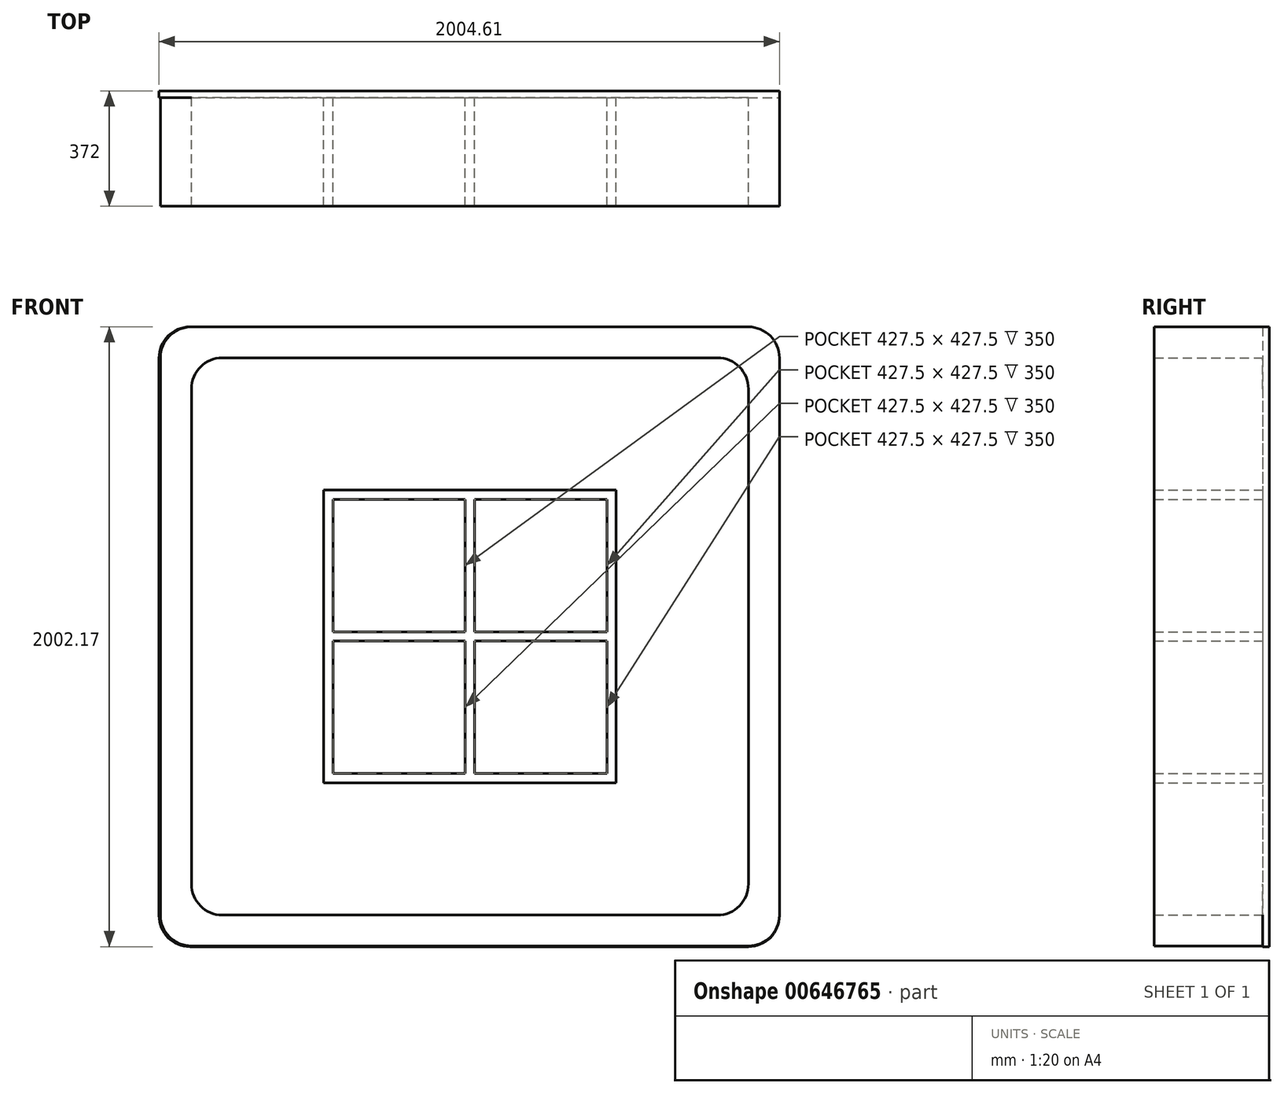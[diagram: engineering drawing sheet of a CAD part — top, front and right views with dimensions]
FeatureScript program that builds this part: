
annotation { "Feature Type Name" : "Feature", "Feature Type Description" : "" }
export const myFeature = defineFeature(function(context is Context, id is Id, definition is map)
    precondition{}
    {
        {
            var Q0;
            Q0=qCreatedBy(makeId("Front.planeOp"),FACE);
            var sketch = newSketch(context, id + "F0", { "sketchPlane" : qUnion([Q0])});
            skLineSegment(sketch, "E0.bottom", {"start": v(-1413.67, 1120.62) * mm, "end": v(386.33, 1120.62) * mm});
            skLineSegment(sketch, "E0.top", {"start": v(-1413.67, -879.38) * mm, "end": v(386.33, -879.38) * mm});
            skLineSegment(sketch, "E0.left", {"start": v(-1513.67, 1020.62) * mm, "end": v(-1513.67, -779.38) * mm});
            skLineSegment(sketch, "E0.right", {"start": v(486.33, 1020.62) * mm, "end": v(486.33, -779.38) * mm});
            skLineSegment(sketch, "E1.bottom", {"start": v(-1313.67, 1020.62) * mm, "end": v(286.33, 1020.62) * mm});
            skLineSegment(sketch, "E1.top", {"start": v(-1313.67, -779.38) * mm, "end": v(286.33, -779.38) * mm});
            skLineSegment(sketch, "E1.left", {"start": v(-1413.67, 920.62) * mm, "end": v(-1413.67, -679.38) * mm});
            skLineSegment(sketch, "E1.right", {"start": v(386.33, 920.62) * mm, "end": v(386.33, -679.38) * mm});
            skPoint(sketch, "E2.visualSharp", {"position": v(-1513.67, 1120.62) * mm});
            skArc(sketch, "E2.filletArc", {"start": v(-1413.67, 1120.62) * mm, "mid": v(-1484.38, 1091.33) * mm, "end": v(-1513.67, 1020.62) * mm});
            skArc(sketch, "E3.filletArc", {"start": v(-1313.67, 1020.62) * mm, "mid": v(-1384.38, 991.33) * mm, "end": v(-1413.67, 920.62) * mm});
            skPoint(sketch, "E4.visualSharp", {"position": v(486.33, 1120.62) * mm});
            skArc(sketch, "E4.filletArc", {"start": v(486.33, 1020.62) * mm, "mid": v(457.05, 1091.33) * mm, "end": v(386.33, 1120.62) * mm});
            skArc(sketch, "E5.filletArc", {"start": v(386.33, 920.62) * mm, "mid": v(357.05, 991.33) * mm, "end": v(286.33, 1020.62) * mm});
            skPoint(sketch, "E6.visualSharp", {"position": v(386.33, -779.38) * mm});
            skArc(sketch, "E6.filletArc", {"start": v(286.33, -779.38) * mm, "mid": v(357.05, -750.1) * mm, "end": v(386.33, -679.38) * mm});
            skPoint(sketch, "E7.visualSharp", {"position": v(-1413.67, -779.38) * mm});
            skArc(sketch, "E7.filletArc", {"start": v(-1413.67, -679.38) * mm, "mid": v(-1384.38, -750.1) * mm, "end": v(-1313.67, -779.38) * mm});
            skPoint(sketch, "E8.visualSharp", {"position": v(-1513.67, -879.38) * mm});
            skArc(sketch, "E8.filletArc", {"start": v(-1513.67, -779.38) * mm, "mid": v(-1484.38, -850.1) * mm, "end": v(-1413.67, -879.38) * mm});
            skPoint(sketch, "E9.visualSharp", {"position": v(486.33, -879.38) * mm});
            skArc(sketch, "E9.filletArc", {"start": v(386.33, -879.38) * mm, "mid": v(457.05, -850.1) * mm, "end": v(486.33, -779.38) * mm});
            skLineSegment(sketch, "E10.bottom", {"start": v(-1413.67, 593.12) * mm, "end": v(386.33, 593.12) * mm});
            skLineSegment(sketch, "E10.top", {"start": v(-1413.67, 563.12) * mm, "end": v(386.33, 563.12) * mm});
            skLineSegment(sketch, "E10.left", {"start": v(-1413.67, 593.12) * mm, "end": v(-1413.67, 563.12) * mm});
            skLineSegment(sketch, "E10.right", {"start": v(386.33, 593.12) * mm, "end": v(386.33, 563.12) * mm});
            skLineSegment(sketch, "E11.bottom", {"start": v(-1413.67, 135.62) * mm, "end": v(386.33, 135.62) * mm});
            skLineSegment(sketch, "E11.top", {"start": v(-1413.67, 105.62) * mm, "end": v(386.33, 105.62) * mm});
            skLineSegment(sketch, "E11.left", {"start": v(-1413.67, 135.62) * mm, "end": v(-1413.67, 105.62) * mm});
            skLineSegment(sketch, "E11.right", {"start": v(386.33, 135.62) * mm, "end": v(386.33, 105.62) * mm});
            skLineSegment(sketch, "E12.bottom", {"start": v(-1413.67, -321.88) * mm, "end": v(386.33, -321.88) * mm});
            skLineSegment(sketch, "E12.top", {"start": v(-1413.67, -351.88) * mm, "end": v(386.33, -351.88) * mm});
            skLineSegment(sketch, "E12.left", {"start": v(-1413.67, -321.88) * mm, "end": v(-1413.67, -351.88) * mm});
            skLineSegment(sketch, "E12.right", {"start": v(386.33, -321.88) * mm, "end": v(386.33, -351.88) * mm});
            skLineSegment(sketch, "E13.bottom", {"start": v(-986.17, 1020.62) * mm, "end": v(-956.17, 1020.62) * mm});
            skLineSegment(sketch, "E13.top", {"start": v(-986.17, -779.38) * mm, "end": v(-956.17, -779.38) * mm});
            skLineSegment(sketch, "E13.left", {"start": v(-986.17, 1020.62) * mm, "end": v(-986.17, -779.38) * mm});
            skLineSegment(sketch, "E13.right", {"start": v(-956.17, 1020.62) * mm, "end": v(-956.17, -779.38) * mm});
            skLineSegment(sketch, "E14.bottom", {"start": v(-528.67, 1020.62) * mm, "end": v(-498.67, 1020.62) * mm});
            skLineSegment(sketch, "E14.top", {"start": v(-528.67, -779.38) * mm, "end": v(-498.67, -779.38) * mm});
            skLineSegment(sketch, "E14.left", {"start": v(-528.67, 1020.62) * mm, "end": v(-528.67, -779.38) * mm});
            skLineSegment(sketch, "E14.right", {"start": v(-498.67, 1020.62) * mm, "end": v(-498.67, -779.38) * mm});
            skLineSegment(sketch, "E15.bottom", {"start": v(-71.17, 1020.62) * mm, "end": v(-41.17, 1020.62) * mm});
            skLineSegment(sketch, "E15.top", {"start": v(-71.17, -779.38) * mm, "end": v(-41.17, -779.38) * mm});
            skLineSegment(sketch, "E15.left", {"start": v(-71.17, 1020.62) * mm, "end": v(-71.17, -779.38) * mm});
            skLineSegment(sketch, "E15.right", {"start": v(-41.17, 1020.62) * mm, "end": v(-41.17, -779.38) * mm});
            skSolve(sketch);
        }
        {
            var Q0;
            Q0=makeQuery(id+"F0.imprint","IMPRINT",FACE,{"disambiguationData":[TD([[makeQuery(id+"F0.imprint","IMPRINT",EDGE,{"derivedFrom":sQuery(id+"F0.wireOp",EDGE,"E0.bottom")}),-1.0]])]});
            var Q1;
            {var subQ0=sQuery(id+"F0.wireOp",EDGE,"E13.right");var subQ1=sQuery(id+"F0.wireOp",EDGE,"E10.bottom");var subQ2=makeQuery(id+"F0.imprint","INTERSECT",VERTEX,{"derivedFrom":[subQ1,subQ0]});Q1=makeQuery(id+"F0.imprint","IMPRINT",FACE,{"disambiguationData":[TD([[makeQuery(id+"F0.imprint","IMPRINT",EDGE,{"disambiguationData":[TD([[subQ2,-1.0]])],"derivedFrom":subQ1}),-1.0]])]});}
            var Q2;
            {var subQ0=sQuery(id+"F0.wireOp",EDGE,"E10.left");Q2=makeQuery(id+"F0.imprint","IMPRINT",FACE,{"disambiguationData":[TD([[makeQuery(id+"F0.imprint","IMPRINT",EDGE,{"derivedFrom":subQ0}),1.0]])]});}
            var Q3;
            {var subQ5=sQuery(id+"F0.wireOp",EDGE,"E13.bottom");Q3=makeQuery(id+"F0.imprint","IMPRINT",FACE,{"disambiguationData":[TD([[makeQuery(id+"F0.imprint","IMPRINT",EDGE,{"derivedFrom":subQ5}),-1.0]])]});}
            var Q4;
            {var subQ0=sQuery(id+"F0.wireOp",EDGE,"E13.left");var subQ1=sQuery(id+"F0.wireOp",EDGE,"E10.bottom");var subQ2=makeQuery(id+"F0.imprint","INTERSECT",VERTEX,{"derivedFrom":[subQ1,subQ0]});Q4=makeQuery(id+"F0.imprint","IMPRINT",FACE,{"disambiguationData":[TD([[makeQuery(id+"F0.imprint","IMPRINT",EDGE,{"disambiguationData":[TD([[subQ2,-1.0]])],"derivedFrom":subQ1}),-1.0]])]});}
            var Q5;
            {var subQ5=sQuery(id+"F0.wireOp",EDGE,"E14.bottom");Q5=makeQuery(id+"F0.imprint","IMPRINT",FACE,{"disambiguationData":[TD([[makeQuery(id+"F0.imprint","IMPRINT",EDGE,{"derivedFrom":subQ5}),-1.0]])]});}
            var Q6;
            {var subQ0=sQuery(id+"F0.wireOp",EDGE,"E14.left");var subQ1=sQuery(id+"F0.wireOp",EDGE,"E10.bottom");var subQ2=makeQuery(id+"F0.imprint","INTERSECT",VERTEX,{"derivedFrom":[subQ1,subQ0]});Q6=makeQuery(id+"F0.imprint","IMPRINT",FACE,{"disambiguationData":[TD([[makeQuery(id+"F0.imprint","IMPRINT",EDGE,{"disambiguationData":[TD([[subQ2,-1.0]])],"derivedFrom":subQ1}),-1.0]])]});}
            var Q7;
            {var subQ0=sQuery(id+"F0.wireOp",EDGE,"E14.right");var subQ1=sQuery(id+"F0.wireOp",EDGE,"E10.bottom");var subQ2=makeQuery(id+"F0.imprint","INTERSECT",VERTEX,{"derivedFrom":[subQ1,subQ0]});Q7=makeQuery(id+"F0.imprint","IMPRINT",FACE,{"disambiguationData":[TD([[makeQuery(id+"F0.imprint","IMPRINT",EDGE,{"disambiguationData":[TD([[subQ2,-1.0]])],"derivedFrom":subQ1}),-1.0]])]});}
            var Q8;
            {var subQ5=sQuery(id+"F0.wireOp",EDGE,"E15.bottom");Q8=makeQuery(id+"F0.imprint","IMPRINT",FACE,{"disambiguationData":[TD([[makeQuery(id+"F0.imprint","IMPRINT",EDGE,{"derivedFrom":subQ5}),-1.0]])]});}
            var Q9;
            {var subQ0=sQuery(id+"F0.wireOp",EDGE,"E15.left");var subQ1=sQuery(id+"F0.wireOp",EDGE,"E10.bottom");var subQ2=makeQuery(id+"F0.imprint","INTERSECT",VERTEX,{"derivedFrom":[subQ1,subQ0]});Q9=makeQuery(id+"F0.imprint","IMPRINT",FACE,{"disambiguationData":[TD([[makeQuery(id+"F0.imprint","IMPRINT",EDGE,{"disambiguationData":[TD([[subQ2,-1.0]])],"derivedFrom":subQ1}),-1.0]])]});}
            var Q10;
            {var subQ0=sQuery(id+"F0.wireOp",EDGE,"E10.right");Q10=makeQuery(id+"F0.imprint","IMPRINT",FACE,{"disambiguationData":[TD([[makeQuery(id+"F0.imprint","IMPRINT",EDGE,{"derivedFrom":subQ0}),-1.0]])]});}
            var Q11;
            {var subQ0=sQuery(id+"F0.wireOp",EDGE,"E15.left");var subQ1=sQuery(id+"F0.wireOp",EDGE,"E10.top");var subQ2=makeQuery(id+"F0.imprint","INTERSECT",VERTEX,{"derivedFrom":[subQ1,subQ0]});Q11=makeQuery(id+"F0.imprint","IMPRINT",FACE,{"disambiguationData":[TD([[makeQuery(id+"F0.imprint","IMPRINT",EDGE,{"disambiguationData":[TD([[subQ2,-1.0]])],"derivedFrom":subQ1}),-1.0]])]});}
            var Q12;
            {var subQ0=sQuery(id+"F0.wireOp",EDGE,"E14.left");var subQ1=sQuery(id+"F0.wireOp",EDGE,"E10.top");var subQ2=makeQuery(id+"F0.imprint","INTERSECT",VERTEX,{"derivedFrom":[subQ1,subQ0]});Q12=makeQuery(id+"F0.imprint","IMPRINT",FACE,{"disambiguationData":[TD([[makeQuery(id+"F0.imprint","IMPRINT",EDGE,{"disambiguationData":[TD([[subQ2,-1.0]])],"derivedFrom":subQ1}),-1.0]])]});}
            var Q13;
            {var subQ0=sQuery(id+"F0.wireOp",EDGE,"E13.left");var subQ1=sQuery(id+"F0.wireOp",EDGE,"E10.top");var subQ2=makeQuery(id+"F0.imprint","INTERSECT",VERTEX,{"derivedFrom":[subQ1,subQ0]});Q13=makeQuery(id+"F0.imprint","IMPRINT",FACE,{"disambiguationData":[TD([[makeQuery(id+"F0.imprint","IMPRINT",EDGE,{"disambiguationData":[TD([[subQ2,-1.0]])],"derivedFrom":subQ1}),-1.0]])]});}
            var Q14;
            {var subQ0=sQuery(id+"F0.wireOp",EDGE,"E11.left");Q14=makeQuery(id+"F0.imprint","IMPRINT",FACE,{"disambiguationData":[TD([[makeQuery(id+"F0.imprint","IMPRINT",EDGE,{"derivedFrom":subQ0}),1.0]])]});}
            var Q15;
            {var subQ0=sQuery(id+"F0.wireOp",EDGE,"E13.left");var subQ1=sQuery(id+"F0.wireOp",EDGE,"E11.bottom");var subQ2=makeQuery(id+"F0.imprint","INTERSECT",VERTEX,{"derivedFrom":[subQ1,subQ0]});Q15=makeQuery(id+"F0.imprint","IMPRINT",FACE,{"disambiguationData":[TD([[makeQuery(id+"F0.imprint","IMPRINT",EDGE,{"disambiguationData":[TD([[subQ2,-1.0]])],"derivedFrom":subQ1}),-1.0]])]});}
            var Q16;
            {var subQ0=sQuery(id+"F0.wireOp",EDGE,"E13.right");var subQ1=sQuery(id+"F0.wireOp",EDGE,"E11.bottom");var subQ2=makeQuery(id+"F0.imprint","INTERSECT",VERTEX,{"derivedFrom":[subQ1,subQ0]});Q16=makeQuery(id+"F0.imprint","IMPRINT",FACE,{"disambiguationData":[TD([[makeQuery(id+"F0.imprint","IMPRINT",EDGE,{"disambiguationData":[TD([[subQ2,-1.0]])],"derivedFrom":subQ1}),-1.0]])]});}
            var Q17;
            {var subQ0=sQuery(id+"F0.wireOp",EDGE,"E14.right");var subQ1=sQuery(id+"F0.wireOp",EDGE,"E11.bottom");var subQ2=makeQuery(id+"F0.imprint","INTERSECT",VERTEX,{"derivedFrom":[subQ1,subQ0]});Q17=makeQuery(id+"F0.imprint","IMPRINT",FACE,{"disambiguationData":[TD([[makeQuery(id+"F0.imprint","IMPRINT",EDGE,{"disambiguationData":[TD([[subQ2,-1.0]])],"derivedFrom":subQ1}),-1.0]])]});}
            var Q18;
            {var subQ0=sQuery(id+"F0.wireOp",EDGE,"E14.left");var subQ1=sQuery(id+"F0.wireOp",EDGE,"E11.bottom");var subQ2=makeQuery(id+"F0.imprint","INTERSECT",VERTEX,{"derivedFrom":[subQ1,subQ0]});Q18=makeQuery(id+"F0.imprint","IMPRINT",FACE,{"disambiguationData":[TD([[makeQuery(id+"F0.imprint","IMPRINT",EDGE,{"disambiguationData":[TD([[subQ2,-1.0]])],"derivedFrom":subQ1}),-1.0]])]});}
            var Q19;
            {var subQ0=sQuery(id+"F0.wireOp",EDGE,"E15.left");var subQ1=sQuery(id+"F0.wireOp",EDGE,"E11.bottom");var subQ2=makeQuery(id+"F0.imprint","INTERSECT",VERTEX,{"derivedFrom":[subQ1,subQ0]});Q19=makeQuery(id+"F0.imprint","IMPRINT",FACE,{"disambiguationData":[TD([[makeQuery(id+"F0.imprint","IMPRINT",EDGE,{"disambiguationData":[TD([[subQ2,-1.0]])],"derivedFrom":subQ1}),-1.0]])]});}
            var Q20;
            {var subQ0=sQuery(id+"F0.wireOp",EDGE,"E11.right");Q20=makeQuery(id+"F0.imprint","IMPRINT",FACE,{"disambiguationData":[TD([[makeQuery(id+"F0.imprint","IMPRINT",EDGE,{"derivedFrom":subQ0}),-1.0]])]});}
            var Q21;
            {var subQ0=sQuery(id+"F0.wireOp",EDGE,"E15.left");var subQ1=sQuery(id+"F0.wireOp",EDGE,"E12.bottom");var subQ2=makeQuery(id+"F0.imprint","INTERSECT",VERTEX,{"derivedFrom":[subQ1,subQ0]});Q21=makeQuery(id+"F0.imprint","IMPRINT",FACE,{"disambiguationData":[TD([[makeQuery(id+"F0.imprint","IMPRINT",EDGE,{"disambiguationData":[TD([[subQ2,-1.0]])],"derivedFrom":subQ1}),-1.0]])]});}
            var Q22;
            {var subQ0=sQuery(id+"F0.wireOp",EDGE,"E14.left");var subQ1=sQuery(id+"F0.wireOp",EDGE,"E12.bottom");var subQ2=makeQuery(id+"F0.imprint","INTERSECT",VERTEX,{"derivedFrom":[subQ1,subQ0]});Q22=makeQuery(id+"F0.imprint","IMPRINT",FACE,{"disambiguationData":[TD([[makeQuery(id+"F0.imprint","IMPRINT",EDGE,{"disambiguationData":[TD([[subQ2,-1.0]])],"derivedFrom":subQ1}),-1.0]])]});}
            var Q23;
            {var subQ0=sQuery(id+"F0.wireOp",EDGE,"E13.left");var subQ1=sQuery(id+"F0.wireOp",EDGE,"E12.bottom");var subQ2=makeQuery(id+"F0.imprint","INTERSECT",VERTEX,{"derivedFrom":[subQ1,subQ0]});Q23=makeQuery(id+"F0.imprint","IMPRINT",FACE,{"disambiguationData":[TD([[makeQuery(id+"F0.imprint","IMPRINT",EDGE,{"disambiguationData":[TD([[subQ2,-1.0]])],"derivedFrom":subQ1}),-1.0]])]});}
            var Q24;
            {var subQ0=sQuery(id+"F0.wireOp",EDGE,"E13.left");var subQ1=sQuery(id+"F0.wireOp",EDGE,"E11.top");var subQ2=makeQuery(id+"F0.imprint","INTERSECT",VERTEX,{"derivedFrom":[subQ1,subQ0]});Q24=makeQuery(id+"F0.imprint","IMPRINT",FACE,{"disambiguationData":[TD([[makeQuery(id+"F0.imprint","IMPRINT",EDGE,{"disambiguationData":[TD([[subQ2,-1.0]])],"derivedFrom":subQ1}),-1.0]])]});}
            var Q25;
            {var subQ0=sQuery(id+"F0.wireOp",EDGE,"E14.left");var subQ1=sQuery(id+"F0.wireOp",EDGE,"E11.top");var subQ2=makeQuery(id+"F0.imprint","INTERSECT",VERTEX,{"derivedFrom":[subQ1,subQ0]});Q25=makeQuery(id+"F0.imprint","IMPRINT",FACE,{"disambiguationData":[TD([[makeQuery(id+"F0.imprint","IMPRINT",EDGE,{"disambiguationData":[TD([[subQ2,-1.0]])],"derivedFrom":subQ1}),-1.0]])]});}
            var Q26;
            {var subQ0=sQuery(id+"F0.wireOp",EDGE,"E13.right");var subQ1=sQuery(id+"F0.wireOp",EDGE,"E12.bottom");var subQ2=makeQuery(id+"F0.imprint","INTERSECT",VERTEX,{"derivedFrom":[subQ1,subQ0]});Q26=makeQuery(id+"F0.imprint","IMPRINT",FACE,{"disambiguationData":[TD([[makeQuery(id+"F0.imprint","IMPRINT",EDGE,{"disambiguationData":[TD([[subQ2,-1.0]])],"derivedFrom":subQ1}),-1.0]])]});}
            var Q27;
            {var subQ0=sQuery(id+"F0.wireOp",EDGE,"E14.right");var subQ1=sQuery(id+"F0.wireOp",EDGE,"E12.bottom");var subQ2=makeQuery(id+"F0.imprint","INTERSECT",VERTEX,{"derivedFrom":[subQ1,subQ0]});Q27=makeQuery(id+"F0.imprint","IMPRINT",FACE,{"disambiguationData":[TD([[makeQuery(id+"F0.imprint","IMPRINT",EDGE,{"disambiguationData":[TD([[subQ2,-1.0]])],"derivedFrom":subQ1}),-1.0]])]});}
            var Q28;
            {var subQ0=sQuery(id+"F0.wireOp",EDGE,"E12.right");Q28=makeQuery(id+"F0.imprint","IMPRINT",FACE,{"disambiguationData":[TD([[makeQuery(id+"F0.imprint","IMPRINT",EDGE,{"derivedFrom":subQ0}),-1.0]])]});}
            var Q29;
            {var subQ0=sQuery(id+"F0.wireOp",EDGE,"E15.left");var subQ1=sQuery(id+"F0.wireOp",EDGE,"E11.top");var subQ2=makeQuery(id+"F0.imprint","INTERSECT",VERTEX,{"derivedFrom":[subQ1,subQ0]});Q29=makeQuery(id+"F0.imprint","IMPRINT",FACE,{"disambiguationData":[TD([[makeQuery(id+"F0.imprint","IMPRINT",EDGE,{"disambiguationData":[TD([[subQ2,-1.0]])],"derivedFrom":subQ1}),-1.0]])]});}
            var Q30;
            {var subQ5=sQuery(id+"F0.wireOp",EDGE,"E15.top");Q30=makeQuery(id+"F0.imprint","IMPRINT",FACE,{"disambiguationData":[TD([[makeQuery(id+"F0.imprint","IMPRINT",EDGE,{"derivedFrom":subQ5}),1.0]])]});}
            var Q31;
            {var subQ5=sQuery(id+"F0.wireOp",EDGE,"E14.top");Q31=makeQuery(id+"F0.imprint","IMPRINT",FACE,{"disambiguationData":[TD([[makeQuery(id+"F0.imprint","IMPRINT",EDGE,{"derivedFrom":subQ5}),1.0]])]});}
            var Q32;
            {var subQ5=sQuery(id+"F0.wireOp",EDGE,"E13.top");Q32=makeQuery(id+"F0.imprint","IMPRINT",FACE,{"disambiguationData":[TD([[makeQuery(id+"F0.imprint","IMPRINT",EDGE,{"derivedFrom":subQ5}),1.0]])]});}
            var Q33;
            {var subQ0=sQuery(id+"F0.wireOp",EDGE,"E12.left");Q33=makeQuery(id+"F0.imprint","IMPRINT",FACE,{"disambiguationData":[TD([[makeQuery(id+"F0.imprint","IMPRINT",EDGE,{"derivedFrom":subQ0}),1.0]])]});}
            extrude(context, id + "F1", {"entities" : qUnion([Q0, Q1, Q2, Q3, Q4, Q5, Q6, Q7, Q8, Q9, Q10, Q11, Q12, Q13, Q14, Q15, Q16, Q17, Q18, Q19, Q20, Q21, Q22, Q23, Q24, Q25, Q26, Q27, Q28, Q29, Q30, Q31, Q32, Q33]), "depth" : 350 * mm, "offsetDistance" : 25 * mm});
        }
        {
            var Q0;
            Q0=makeQuery(id+"F1.opExtrude","CAP_FACE",FACE,{"disambiguationData":[OSD([sQuery(id+"F0.wireOp",EDGE,"E0.bottom"),sQuery(id+"F0.wireOp",EDGE,"E0.top"),sQuery(id+"F0.wireOp",EDGE,"E0.left"),sQuery(id+"F0.wireOp",EDGE,"E0.right"),sQuery(id+"F0.wireOp",EDGE,"E1.bottom"),sQuery(id+"F0.wireOp",EDGE,"E1.top"),sQuery(id+"F0.wireOp",EDGE,"E1.left"),sQuery(id+"F0.wireOp",EDGE,"E1.right"),sQuery(id+"F0.wireOp",EDGE,"E2.filletArc"),sQuery(id+"F0.wireOp",EDGE,"E3.filletArc"),sQuery(id+"F0.wireOp",EDGE,"E4.filletArc"),sQuery(id+"F0.wireOp",EDGE,"E5.filletArc"),sQuery(id+"F0.wireOp",EDGE,"E6.filletArc"),sQuery(id+"F0.wireOp",EDGE,"E7.filletArc"),sQuery(id+"F0.wireOp",EDGE,"E8.filletArc"),sQuery(id+"F0.wireOp",EDGE,"E9.filletArc"),sQuery(id+"F0.wireOp",EDGE,"E10.bottom"),sQuery(id+"F0.wireOp",EDGE,"E10.top"),sQuery(id+"F0.wireOp",EDGE,"E11.bottom"),sQuery(id+"F0.wireOp",EDGE,"E11.top"),sQuery(id+"F0.wireOp",EDGE,"E12.bottom"),sQuery(id+"F0.wireOp",EDGE,"E12.top"),sQuery(id+"F0.wireOp",EDGE,"E13.left"),sQuery(id+"F0.wireOp",EDGE,"E13.right"),sQuery(id+"F0.wireOp",EDGE,"E14.left"),sQuery(id+"F0.wireOp",EDGE,"E14.right"),sQuery(id+"F0.wireOp",EDGE,"E15.left"),sQuery(id+"F0.wireOp",EDGE,"E15.right")])],"isStart":true});
            var sketch = newSketch(context, id + "F2", { "sketchPlane" : qUnion([Q0])});
            skLineSegment(sketch, "E16.bottom", {"start": v(-386.33, 1120.62) * mm, "end": v(1418.28, 1120.62) * mm});
            skLineSegment(sketch, "E16.top", {"start": v(-386.33, -881.55) * mm, "end": v(1418.28, -881.55) * mm});
            skLineSegment(sketch, "E16.left", {"start": v(-486.33, 1020.62) * mm, "end": v(-486.33, -781.55) * mm});
            skLineSegment(sketch, "E16.right", {"start": v(1518.28, 1020.62) * mm, "end": v(1518.28, -781.55) * mm});
            skPoint(sketch, "E17.visualSharp", {"position": v(-486.33, 1120.62) * mm});
            skArc(sketch, "E17.filletArc", {"start": v(-386.33, 1120.62) * mm, "mid": v(-457.05, 1091.33) * mm, "end": v(-486.33, 1020.62) * mm});
            skPoint(sketch, "E18.visualSharp", {"position": v(1518.28, 1120.62) * mm});
            skArc(sketch, "E18.filletArc", {"start": v(1518.28, 1020.62) * mm, "mid": v(1489, 1091.33) * mm, "end": v(1418.28, 1120.62) * mm});
            skPoint(sketch, "E19.visualSharp", {"position": v(1518.28, -881.55) * mm});
            skArc(sketch, "E19.filletArc", {"start": v(1418.28, -881.55) * mm, "mid": v(1489, -852.26) * mm, "end": v(1518.28, -781.55) * mm});
            skPoint(sketch, "E20.visualSharp", {"position": v(-486.33, -881.55) * mm});
            skArc(sketch, "E20.filletArc", {"start": v(-486.33, -781.55) * mm, "mid": v(-457.05, -852.26) * mm, "end": v(-386.33, -881.55) * mm});
            skSolve(sketch);
        }
        {
            var Q0;
            Q0 = qSketchRegion(id + "F2", true);
            extrude(context, id + "F3", {"entities" : qUnion([Q0]), "operationType" : NewBodyOperationType.ADD, "depth" : 22 * mm, "offsetDistance" : 25 * mm});
        }
    });
